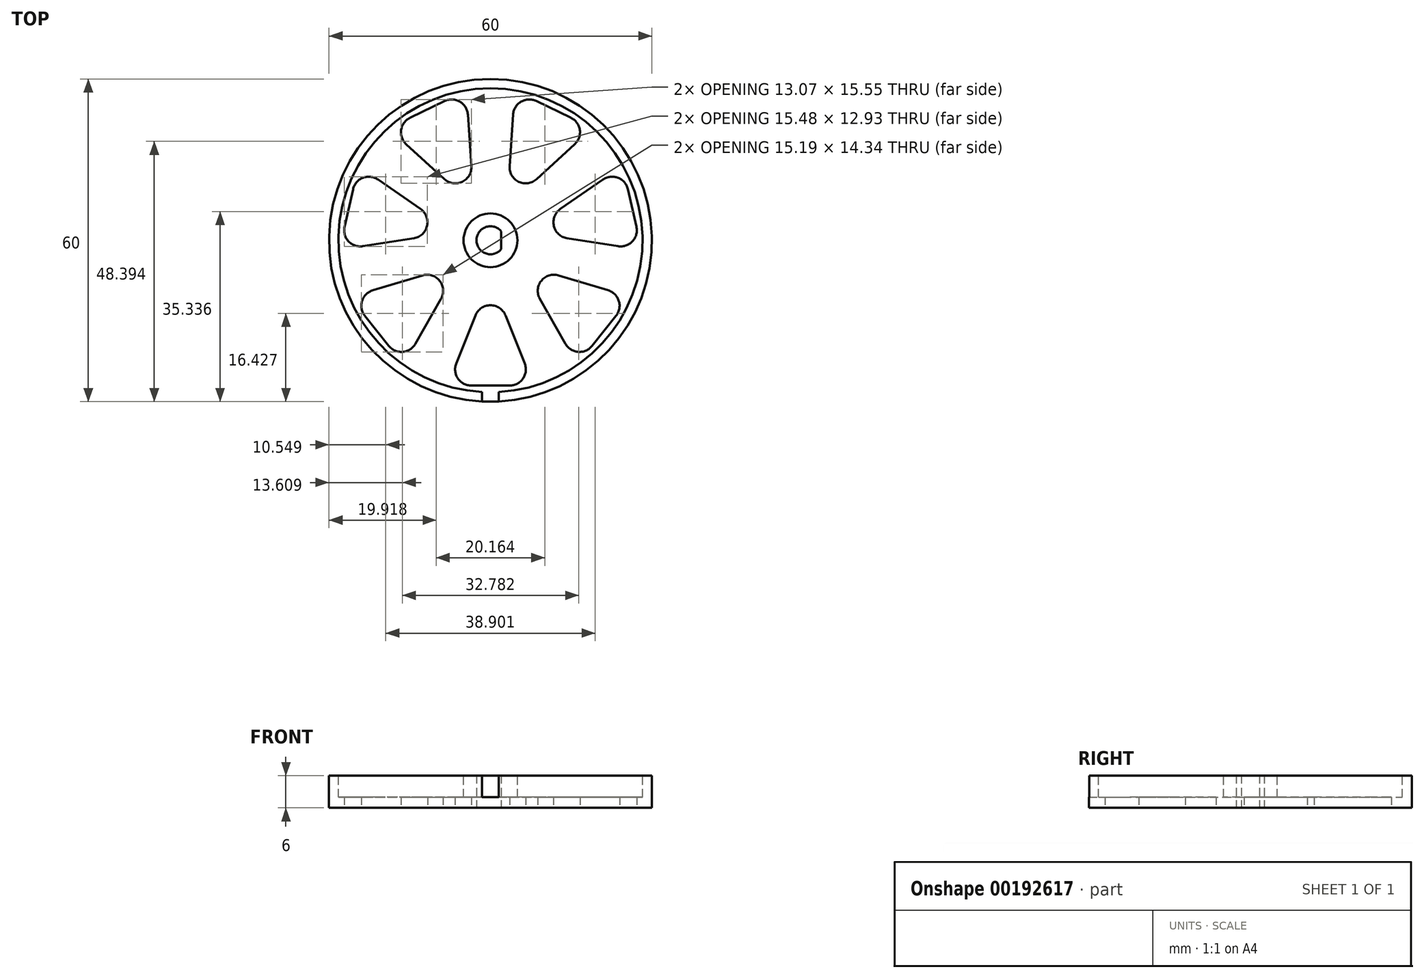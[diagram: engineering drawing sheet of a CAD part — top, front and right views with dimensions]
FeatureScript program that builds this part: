
annotation { "Feature Type Name" : "Feature", "Feature Type Description" : "" }
export const myFeature = defineFeature(function(context is Context, id is Id, definition is map)
    precondition{}
    {
        {
            var Q0;
            Q0=qCreatedBy(makeId("Top.planeOp"),FACE);
            var sketch = newSketch(context, id + "F0", { "sketchPlane" : qUnion([Q0])});
            skCircle(sketch, "E0", {"center": v(0, 0) * mm, "radius": 30 * mm});
            skCircle(sketch, "E1", {"center": v(0, 0) * mm, "radius": 2.6 * mm});
            skLineSegment(sketch, "E2", {"start": v(2, -1.66) * mm, "end": v(2, 1.66) * mm});
            skSolve(sketch);
        }
        {
            var Q0;
            Q0=makeQuery(id+"F0.imprint","IMPRINT",FACE,{"disambiguationData":[TD([[makeQuery(id+"F0.imprint","IMPRINT",EDGE,{"derivedFrom":sQuery(id+"F0.wireOp",EDGE,"E0")}),1.0]])]});
            var Q1;
            {var subQ0=sQuery(id+"F0.wireOp",EDGE,"E2");Q1=makeQuery(id+"F0.imprint","IMPRINT",FACE,{"disambiguationData":[TD([[makeQuery(id+"F0.imprint","IMPRINT",EDGE,{"derivedFrom":subQ0}),-1.0]])]});}
            extrude(context, id + "F1", {"entities" : qUnion([Q0, Q1]), "depth" : 6 * mm});
        }
        {
            var Q0;
            Q0=makeQuery(id+"F1.opExtrude","CAP_FACE",FACE,{"disambiguationData":[OSD([sQuery(id+"F0.wireOp",EDGE,"E0"),sQuery(id+"F0.wireOp",EDGE,"E1"),sQuery(id+"F0.wireOp",EDGE,"E2")])],"isStart":false});
            var sketch = newSketch(context, id + "F2", { "sketchPlane" : qUnion([Q0])});
            skCircle(sketch, "E3", {"center": v(0, 0) * mm, "radius": 5 * mm});
            skCircle(sketch, "E4", {"center": v(0, 0) * mm, "radius": 28.25 * mm});
            skCircle(sketch, "E5.0", {"center": v(0, 0) * mm, "radius": 30 * mm});
            skSolve(sketch);
        }
        {
            var Q0;
            Q0=makeQuery(id+"F2.imprint","IMPRINT",FACE,{"disambiguationData":[TD([[makeQuery(id+"F2.imprint","IMPRINT",EDGE,{"derivedFrom":sQuery(id+"F2.wireOp",EDGE,"E3")}),-1.0]])]});
            extrude(context, id + "F3", {"entities" : qUnion([Q0]), "operationType" : NewBodyOperationType.REMOVE, "oppositeDirection" : true, "depth" : 4 * mm});
        }
        {
            var Q0;
            Q0=qCreatedBy(makeId("Front.planeOp"),FACE);
            cPlane(context, id + "F4", {"entities" : qUnion([Q0]), "cplaneType" : CPlaneType.OFFSET, "offset" : 25 * mm, "width" : 150 * mm, "height" : 150 * mm});
        }
        {
            var Q0;
            Q0=qCreatedBy(id+"F4.planeOp",FACE);
            var sketch = newSketch(context, id + "F5", { "sketchPlane" : qUnion([Q0])});
            skLineSegment(sketch, "E6.0", {"start": v(-30, 6) * mm, "end": v(30, 6) * mm});
            skLineSegment(sketch, "E7.bottom", {"start": v(1.55, 2) * mm, "end": v(-1.55, 2) * mm});
            skLineSegment(sketch, "E7.top", {"start": v(1.55, 10) * mm, "end": v(-1.55, 10) * mm});
            skLineSegment(sketch, "E7.left", {"start": v(1.55, 2) * mm, "end": v(1.55, 10) * mm});
            skLineSegment(sketch, "E7.right", {"start": v(-1.55, 2) * mm, "end": v(-1.55, 10) * mm});
            skPoint(sketch, "E7.middle", {"position": v(0, 6) * mm});
            skSolve(sketch);
        }
        {
            var Q0;
            Q0 = qSketchRegion(id + "F5", true);
            extrude(context, id + "F6", {"entities" : qUnion([Q0]), "operationType" : NewBodyOperationType.REMOVE, "depth" : 25 * mm});
        }
        {
            var Q0;
            Q0=makeQuery(id+"F1.opExtrude","CAP_FACE",FACE,{"disambiguationData":[OSD([sQuery(id+"F0.wireOp",EDGE,"E0"),sQuery(id+"F0.wireOp",EDGE,"E1"),sQuery(id+"F0.wireOp",EDGE,"E2")])],"isStart":true});
            var sketch = newSketch(context, id + "F7", { "sketchPlane" : qUnion([Q0])});
            skCircle(sketch, "E8.0", {"center": v(0, 0) * mm, "radius": 30 * mm, "construction": true});
            skLineSegment(sketch, "E9", {"start": v(2.79, 13.96) * mm, "end": v(6.35, 22.89) * mm});
            skLineSegment(sketch, "E10", {"start": v(3.57, 27) * mm, "end": v(0, 27) * mm});
            skLineSegment(sketch, "E11", {"start": v(0, 27) * mm, "end": v(-3.57, 27) * mm});
            skLineSegment(sketch, "E12", {"start": v(-6.35, 22.89) * mm, "end": v(-2.79, 13.96) * mm});
            skLineSegment(sketch, "E13.1.0", {"start": v(-18.88, 19.62) * mm, "end": v(-21.11, 16.83) * mm});
            skLineSegment(sketch, "E13.1.1", {"start": v(-21.11, 16.83) * mm, "end": v(-23.34, 14.04) * mm});
            skLineSegment(sketch, "E13.1.2", {"start": v(-21.86, 9.3) * mm, "end": v(-12.65, 6.53) * mm});
            skLineSegment(sketch, "E13.1.3", {"start": v(-9.18, 10.88) * mm, "end": v(-13.93, 19.24) * mm});
            skLineSegment(sketch, "E13.2.0", {"start": v(-27.12, -2.53) * mm, "end": v(-26.32, -6) * mm});
            skLineSegment(sketch, "E13.2.1", {"start": v(-26.32, -6) * mm, "end": v(-25.53, -9.49) * mm});
            skLineSegment(sketch, "E13.2.2", {"start": v(-20.9, -11.29) * mm, "end": v(-13, -5.82) * mm});
            skLineSegment(sketch, "E13.2.3", {"start": v(-14.23, -0.4) * mm, "end": v(-23.73, 1.1) * mm});
            skLineSegment(sketch, "E13.3.0", {"start": v(-14.93, -22.78) * mm, "end": v(-11.72, -24.33) * mm});
            skLineSegment(sketch, "E13.3.1", {"start": v(-11.72, -24.33) * mm, "end": v(-8.5, -25.88) * mm});
            skLineSegment(sketch, "E13.3.2", {"start": v(-4.2, -23.38) * mm, "end": v(-3.55, -13.79) * mm});
            skLineSegment(sketch, "E13.3.3", {"start": v(-8.57, -11.37) * mm, "end": v(-15.66, -17.86) * mm});
            skLineSegment(sketch, "E13.4.0", {"start": v(8.5, -25.88) * mm, "end": v(11.72, -24.33) * mm});
            skLineSegment(sketch, "E13.4.1", {"start": v(11.72, -24.33) * mm, "end": v(14.93, -22.78) * mm});
            skLineSegment(sketch, "E13.4.2", {"start": v(15.66, -17.86) * mm, "end": v(8.57, -11.37) * mm});
            skLineSegment(sketch, "E13.4.3", {"start": v(3.55, -13.79) * mm, "end": v(4.2, -23.38) * mm});
            skLineSegment(sketch, "E13.5.0", {"start": v(25.53, -9.49) * mm, "end": v(26.32, -6) * mm});
            skLineSegment(sketch, "E13.5.1", {"start": v(26.32, -6) * mm, "end": v(27.12, -2.53) * mm});
            skLineSegment(sketch, "E13.5.2", {"start": v(23.73, 1.1) * mm, "end": v(14.23, -0.4) * mm});
            skLineSegment(sketch, "E13.5.3", {"start": v(13, -5.82) * mm, "end": v(20.9, -11.29) * mm});
            skLineSegment(sketch, "E13.6.0", {"start": v(23.34, 14.04) * mm, "end": v(21.11, 16.83) * mm});
            skLineSegment(sketch, "E13.6.1", {"start": v(21.11, 16.83) * mm, "end": v(18.88, 19.62) * mm});
            skLineSegment(sketch, "E13.6.2", {"start": v(13.93, 19.24) * mm, "end": v(9.18, 10.88) * mm});
            skLineSegment(sketch, "E13.6.3", {"start": v(12.65, 6.53) * mm, "end": v(21.86, 9.3) * mm});
            skPoint(sketch, "E14.visualSharp", {"position": v(-24.54, -13.8) * mm});
            skArc(sketch, "E14.filletArc", {"start": v(-25.53, -9.49) * mm, "mid": v(-23.7, -11.62) * mm, "end": v(-20.9, -11.29) * mm});
            skPoint(sketch, "E15.visualSharp", {"position": v(-28.1, 1.8) * mm});
            skArc(sketch, "E15.filletArc", {"start": v(-23.73, 1.1) * mm, "mid": v(-26.39, 0.19) * mm, "end": v(-27.12, -2.53) * mm});
            skPoint(sketch, "E16.visualSharp", {"position": v(-18.92, -20.86) * mm});
            skArc(sketch, "E16.filletArc", {"start": v(-15.66, -17.86) * mm, "mid": v(-16.6, -20.51) * mm, "end": v(-14.93, -22.78) * mm});
            skPoint(sketch, "E17.visualSharp", {"position": v(-4.5, -27.8) * mm});
            skArc(sketch, "E17.filletArc", {"start": v(-8.5, -25.88) * mm, "mid": v(-5.69, -25.77) * mm, "end": v(-4.2, -23.38) * mm});
            skPoint(sketch, "E18.visualSharp", {"position": v(4.5, -27.8) * mm});
            skArc(sketch, "E18.filletArc", {"start": v(4.2, -23.38) * mm, "mid": v(5.69, -25.77) * mm, "end": v(8.5, -25.88) * mm});
            skPoint(sketch, "E19.visualSharp", {"position": v(18.92, -20.86) * mm});
            skArc(sketch, "E19.filletArc", {"start": v(14.93, -22.78) * mm, "mid": v(16.6, -20.51) * mm, "end": v(15.66, -17.86) * mm});
            skPoint(sketch, "E20.visualSharp", {"position": v(24.54, -13.8) * mm});
            skArc(sketch, "E20.filletArc", {"start": v(20.9, -11.29) * mm, "mid": v(23.7, -11.62) * mm, "end": v(25.53, -9.49) * mm});
            skPoint(sketch, "E21.visualSharp", {"position": v(28.1, 1.8) * mm});
            skArc(sketch, "E21.filletArc", {"start": v(27.12, -2.53) * mm, "mid": v(26.39, 0.19) * mm, "end": v(23.73, 1.1) * mm});
            skPoint(sketch, "E22.visualSharp", {"position": v(26.1, 10.58) * mm});
            skArc(sketch, "E22.filletArc", {"start": v(21.86, 9.3) * mm, "mid": v(23.85, 11.28) * mm, "end": v(23.34, 14.04) * mm});
            skPoint(sketch, "E23.visualSharp", {"position": v(16.12, 23.09) * mm});
            skArc(sketch, "E23.filletArc", {"start": v(18.88, 19.62) * mm, "mid": v(16.3, 20.75) * mm, "end": v(13.93, 19.24) * mm});
            skPoint(sketch, "E24.visualSharp", {"position": v(8, 27) * mm});
            skArc(sketch, "E24.filletArc", {"start": v(6.35, 22.89) * mm, "mid": v(6.05, 25.68) * mm, "end": v(3.57, 27) * mm});
            skPoint(sketch, "E25.visualSharp", {"position": v(-8, 27) * mm});
            skArc(sketch, "E25.filletArc", {"start": v(-3.57, 27) * mm, "mid": v(-6.05, 25.68) * mm, "end": v(-6.35, 22.89) * mm});
            skPoint(sketch, "E26.visualSharp", {"position": v(-16.12, 23.09) * mm});
            skArc(sketch, "E26.filletArc", {"start": v(-13.93, 19.24) * mm, "mid": v(-16.3, 20.75) * mm, "end": v(-18.88, 19.62) * mm});
            skPoint(sketch, "E27.visualSharp", {"position": v(-26.1, 10.58) * mm});
            skArc(sketch, "E27.filletArc", {"start": v(-23.34, 14.04) * mm, "mid": v(-23.85, 11.28) * mm, "end": v(-21.86, 9.3) * mm});
            skPoint(sketch, "E28.visualSharp", {"position": v(-6.83, -1.56) * mm});
            skArc(sketch, "E28.filletArc", {"start": v(-13, -5.82) * mm, "mid": v(-11.78, -2.69) * mm, "end": v(-14.23, -0.4) * mm});
            skPoint(sketch, "E29.visualSharp", {"position": v(-3.04, -6.3) * mm});
            skArc(sketch, "E29.filletArc", {"start": v(-3.55, -13.79) * mm, "mid": v(-5.24, -10.88) * mm, "end": v(-8.57, -11.37) * mm});
            skPoint(sketch, "E30.visualSharp", {"position": v(3.04, -6.3) * mm});
            skArc(sketch, "E30.filletArc", {"start": v(8.57, -11.37) * mm, "mid": v(5.24, -10.88) * mm, "end": v(3.55, -13.79) * mm});
            skPoint(sketch, "E31.visualSharp", {"position": v(6.83, -1.56) * mm});
            skArc(sketch, "E31.filletArc", {"start": v(14.23, -0.4) * mm, "mid": v(11.78, -2.69) * mm, "end": v(13, -5.82) * mm});
            skPoint(sketch, "E32.visualSharp", {"position": v(5.47, 4.36) * mm});
            skArc(sketch, "E32.filletArc", {"start": v(9.18, 10.88) * mm, "mid": v(9.44, 7.53) * mm, "end": v(12.65, 6.53) * mm});
            skPoint(sketch, "E33.visualSharp", {"position": v(0, 7) * mm});
            skArc(sketch, "E33.filletArc", {"start": v(-2.79, 13.96) * mm, "mid": v(0, 12.08) * mm, "end": v(2.79, 13.96) * mm});
            skPoint(sketch, "E34.visualSharp", {"position": v(-5.47, 4.36) * mm});
            skArc(sketch, "E34.filletArc", {"start": v(-12.65, 6.53) * mm, "mid": v(-9.44, 7.53) * mm, "end": v(-9.18, 10.88) * mm});
            skSolve(sketch);
        }
        {
            var Q0;
            Q0=makeQuery(id+"F7.imprint","IMPRINT",FACE,{"disambiguationData":[TD([[makeQuery(id+"F7.imprint","IMPRINT",EDGE,{"derivedFrom":sQuery(id+"F7.wireOp",EDGE,"E9")}),1.0]])]});
            var Q1;
            Q1=makeQuery(id+"F7.imprint","IMPRINT",FACE,{"disambiguationData":[TD([[makeQuery(id+"F7.imprint","IMPRINT",EDGE,{"derivedFrom":sQuery(id+"F7.wireOp",EDGE,"E13.6.0")}),1.0]])]});
            var Q2;
            Q2=makeQuery(id+"F7.imprint","IMPRINT",FACE,{"disambiguationData":[TD([[makeQuery(id+"F7.imprint","IMPRINT",EDGE,{"derivedFrom":sQuery(id+"F7.wireOp",EDGE,"E13.5.0")}),1.0]])]});
            var Q3;
            Q3=makeQuery(id+"F7.imprint","IMPRINT",FACE,{"disambiguationData":[TD([[makeQuery(id+"F7.imprint","IMPRINT",EDGE,{"derivedFrom":sQuery(id+"F7.wireOp",EDGE,"E13.4.0")}),1.0]])]});
            var Q4;
            Q4=makeQuery(id+"F7.imprint","IMPRINT",FACE,{"disambiguationData":[TD([[makeQuery(id+"F7.imprint","IMPRINT",EDGE,{"derivedFrom":sQuery(id+"F7.wireOp",EDGE,"E13.3.0")}),1.0]])]});
            var Q5;
            Q5=makeQuery(id+"F7.imprint","IMPRINT",FACE,{"disambiguationData":[TD([[makeQuery(id+"F7.imprint","IMPRINT",EDGE,{"derivedFrom":sQuery(id+"F7.wireOp",EDGE,"E13.2.0")}),1.0]])]});
            var Q6;
            Q6=makeQuery(id+"F7.imprint","IMPRINT",FACE,{"disambiguationData":[TD([[makeQuery(id+"F7.imprint","IMPRINT",EDGE,{"derivedFrom":sQuery(id+"F7.wireOp",EDGE,"E13.1.0")}),1.0]])]});
            extrude(context, id + "F8", {"entities" : qUnion([Q0, Q1, Q2, Q3, Q4, Q5, Q6]), "operationType" : NewBodyOperationType.REMOVE, "oppositeDirection" : true, "depth" : 25 * mm});
        }
    });
